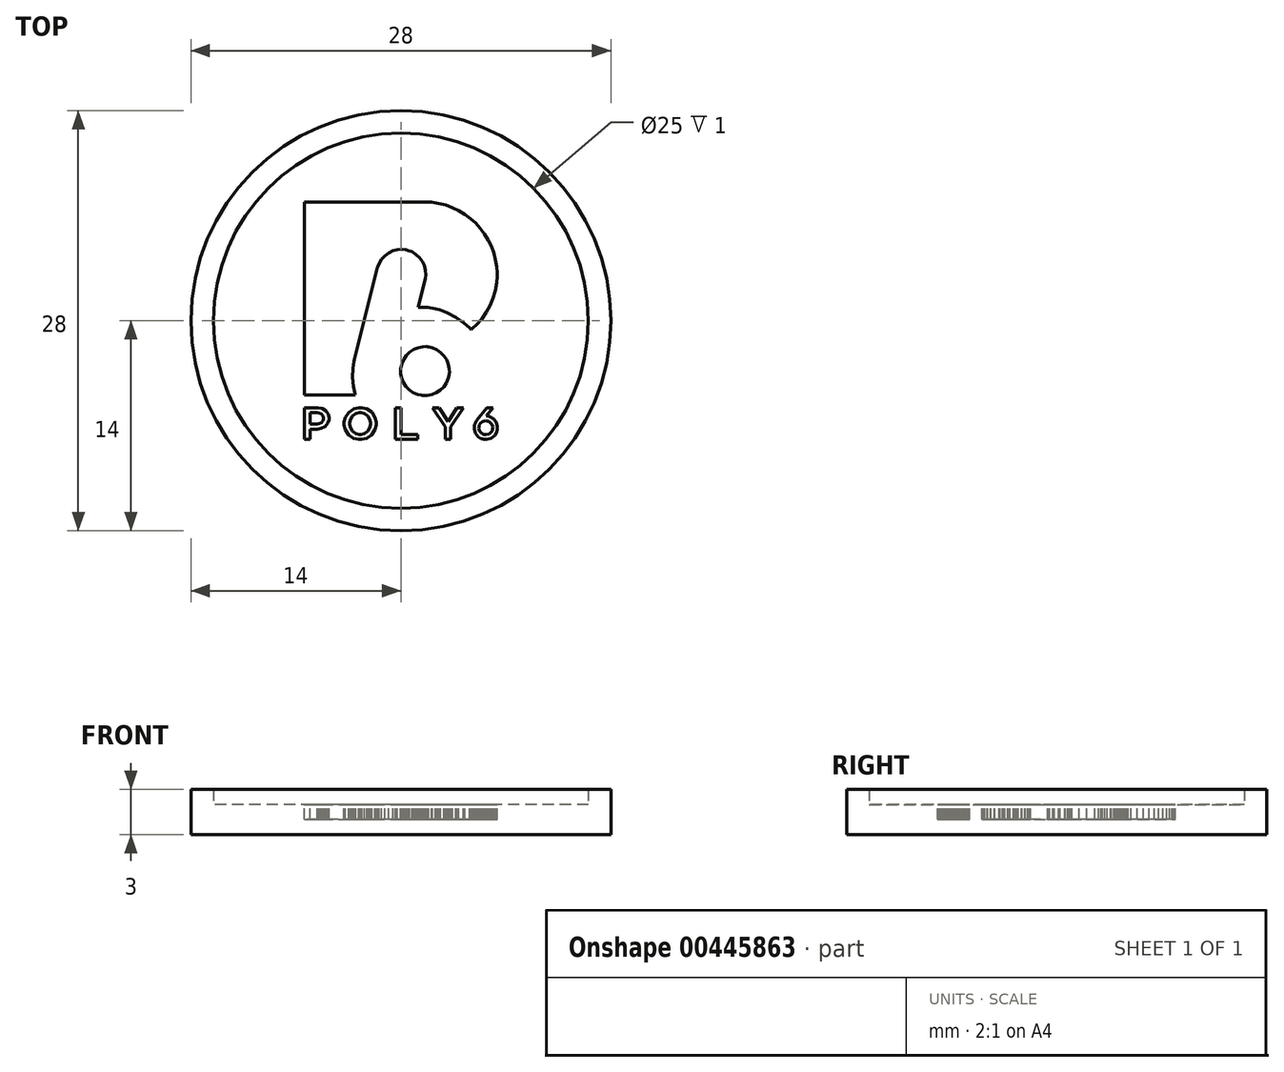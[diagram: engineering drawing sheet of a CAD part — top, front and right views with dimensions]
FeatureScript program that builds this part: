
annotation { "Feature Type Name" : "Feature", "Feature Type Description" : "" }
export const myFeature = defineFeature(function(context is Context, id is Id, definition is map)
    precondition{}
    {
        {
            var Q0;
            Q0=qCreatedBy(makeId("Top.planeOp"),FACE);
            var sketch = newSketch(context, id + "F0", { "sketchPlane" : qUnion([Q0])});
            skCircle(sketch, "E0", {"center": v(0, 0) * mm, "radius": 12.5 * mm});
            skSolve(sketch);
        }
        {
            var Q0;
            Q0=qCreatedBy(makeId("Top.planeOp"),FACE);
            var sketch = newSketch(context, id + "F1", { "sketchPlane" : qUnion([Q0])});
            skLineSegment(sketch, "E1", {"start": v(2.95, -7.92) * mm, "end": v(3.33, -7.92) * mm});
            skLineSegment(sketch, "E2", {"start": v(3.33, -7.92) * mm, "end": v(3.33, -7.07) * mm});
            skLineSegment(sketch, "E3", {"start": v(3.33, -7.07) * mm, "end": v(4.17, -5.8) * mm});
            skLineSegment(sketch, "E4", {"start": v(4.17, -5.8) * mm, "end": v(3.74, -5.8) * mm});
            skLineSegment(sketch, "E5", {"start": v(3.74, -5.8) * mm, "end": v(3.14, -6.73) * mm});
            skLineSegment(sketch, "E6", {"start": v(3.14, -6.73) * mm, "end": v(2.55, -5.8) * mm});
            skLineSegment(sketch, "E7", {"start": v(2.55, -5.8) * mm, "end": v(2.1, -5.8) * mm});
            skLineSegment(sketch, "E8", {"start": v(2.1, -5.8) * mm, "end": v(2.95, -7.08) * mm});
            skLineSegment(sketch, "E9", {"start": v(2.95, -7.08) * mm, "end": v(2.95, -7.92) * mm});
            skLineSegment(sketch, "E10", {"start": v(-0.38, -7.92) * mm, "end": v(1.11, -7.92) * mm});
            skLineSegment(sketch, "E11", {"start": v(1.11, -7.92) * mm, "end": v(1.11, -7.58) * mm});
            skLineSegment(sketch, "E12", {"start": v(1.11, -7.58) * mm, "end": v(0, -7.58) * mm});
            skLineSegment(sketch, "E13", {"start": v(0, -7.58) * mm, "end": v(0, -5.8) * mm});
            skLineSegment(sketch, "E14", {"start": v(0, -5.8) * mm, "end": v(-0.38, -5.8) * mm});
            skLineSegment(sketch, "E15", {"start": v(-0.38, -5.8) * mm, "end": v(-0.38, -7.92) * mm});
            skLineSegment(sketch, "E16", {"start": v(-2.71, -7.59) * mm, "end": v(-2.78, -7.59) * mm});
            skLineSegment(sketch, "E17", {"start": v(-2.78, -7.59) * mm, "end": v(-3, -7.53) * mm});
            skLineSegment(sketch, "E18", {"start": v(-3, -7.53) * mm, "end": v(-3.21, -7.37) * mm});
            skLineSegment(sketch, "E19", {"start": v(-3.21, -7.37) * mm, "end": v(-3.36, -7.14) * mm});
            skLineSegment(sketch, "E20", {"start": v(-3.36, -7.14) * mm, "end": v(-3.4, -6.93) * mm});
            skLineSegment(sketch, "E21", {"start": v(-3.4, -6.93) * mm, "end": v(-3.4, -6.86) * mm});
            skLineSegment(sketch, "E22", {"start": v(-3.4, -6.86) * mm, "end": v(-3.4, -6.85) * mm});
            skLineSegment(sketch, "E23", {"start": v(-3.4, -6.85) * mm, "end": v(-3.4, -6.78) * mm});
            skLineSegment(sketch, "E24", {"start": v(-3.4, -6.78) * mm, "end": v(-3.36, -6.57) * mm});
            skLineSegment(sketch, "E25", {"start": v(-3.36, -6.57) * mm, "end": v(-3.22, -6.34) * mm});
            skLineSegment(sketch, "E26", {"start": v(-3.22, -6.34) * mm, "end": v(-3, -6.19) * mm});
            skLineSegment(sketch, "E27", {"start": v(-3, -6.19) * mm, "end": v(-2.79, -6.13) * mm});
            skLineSegment(sketch, "E28", {"start": v(-2.79, -6.13) * mm, "end": v(-2.72, -6.13) * mm});
            skLineSegment(sketch, "E29", {"start": v(-2.72, -6.13) * mm, "end": v(-2.65, -6.13) * mm});
            skLineSegment(sketch, "E30", {"start": v(-2.65, -6.13) * mm, "end": v(-2.44, -6.19) * mm});
            skLineSegment(sketch, "E31", {"start": v(-2.44, -6.19) * mm, "end": v(-2.22, -6.34) * mm});
            skLineSegment(sketch, "E32", {"start": v(-2.22, -6.34) * mm, "end": v(-2.07, -6.58) * mm});
            skLineSegment(sketch, "E33", {"start": v(-2.07, -6.58) * mm, "end": v(-2.02, -6.79) * mm});
            skLineSegment(sketch, "E34", {"start": v(-2.02, -6.79) * mm, "end": v(-2.02, -6.86) * mm});
            skLineSegment(sketch, "E35", {"start": v(-2.02, -6.86) * mm, "end": v(-2.02, -6.86) * mm});
            skLineSegment(sketch, "E36", {"start": v(-2.02, -6.86) * mm, "end": v(-2.02, -6.93) * mm});
            skLineSegment(sketch, "E37", {"start": v(-2.02, -6.93) * mm, "end": v(-2.07, -7.14) * mm});
            skLineSegment(sketch, "E38", {"start": v(-2.07, -7.14) * mm, "end": v(-2.21, -7.37) * mm});
            skLineSegment(sketch, "E39", {"start": v(-2.21, -7.37) * mm, "end": v(-2.43, -7.53) * mm});
            skLineSegment(sketch, "E40", {"start": v(-2.43, -7.53) * mm, "end": v(-2.64, -7.59) * mm});
            skLineSegment(sketch, "E41", {"start": v(-2.64, -7.59) * mm, "end": v(-2.71, -7.59) * mm});
            skLineSegment(sketch, "E42", {"start": v(-2.72, -7.92) * mm, "end": v(-2.6, -7.92) * mm});
            skLineSegment(sketch, "E43", {"start": v(-2.6, -7.92) * mm, "end": v(-2.28, -7.83) * mm});
            skLineSegment(sketch, "E44", {"start": v(-2.28, -7.83) * mm, "end": v(-1.94, -7.6) * mm});
            skLineSegment(sketch, "E45", {"start": v(-1.94, -7.6) * mm, "end": v(-1.72, -7.27) * mm});
            skLineSegment(sketch, "E46", {"start": v(-1.72, -7.27) * mm, "end": v(-1.64, -6.96) * mm});
            skLineSegment(sketch, "E47", {"start": v(-1.64, -6.96) * mm, "end": v(-1.64, -6.86) * mm});
            skLineSegment(sketch, "E48", {"start": v(-1.64, -6.86) * mm, "end": v(-1.64, -6.85) * mm});
            skLineSegment(sketch, "E49", {"start": v(-1.64, -6.85) * mm, "end": v(-1.64, -6.75) * mm});
            skLineSegment(sketch, "E50", {"start": v(-1.64, -6.75) * mm, "end": v(-1.72, -6.44) * mm});
            skLineSegment(sketch, "E51", {"start": v(-1.72, -6.44) * mm, "end": v(-1.94, -6.1) * mm});
            skLineSegment(sketch, "E52", {"start": v(-1.94, -6.1) * mm, "end": v(-2.28, -5.88) * mm});
            skLineSegment(sketch, "E53", {"start": v(-2.28, -5.88) * mm, "end": v(-2.6, -5.8) * mm});
            skLineSegment(sketch, "E54", {"start": v(-2.6, -5.8) * mm, "end": v(-2.71, -5.8) * mm});
            skLineSegment(sketch, "E55", {"start": v(-2.71, -5.8) * mm, "end": v(-2.82, -5.8) * mm});
            skLineSegment(sketch, "E56", {"start": v(-2.82, -5.8) * mm, "end": v(-3.14, -5.88) * mm});
            skLineSegment(sketch, "E57", {"start": v(-3.14, -5.88) * mm, "end": v(-3.49, -6.11) * mm});
            skLineSegment(sketch, "E58", {"start": v(-3.49, -6.11) * mm, "end": v(-3.7, -6.45) * mm});
            skLineSegment(sketch, "E59", {"start": v(-3.7, -6.45) * mm, "end": v(-3.79, -6.76) * mm});
            skLineSegment(sketch, "E60", {"start": v(-3.79, -6.76) * mm, "end": v(-3.79, -6.86) * mm});
            skLineSegment(sketch, "E61", {"start": v(-3.79, -6.86) * mm, "end": v(-3.79, -6.86) * mm});
            skLineSegment(sketch, "E62", {"start": v(-3.79, -6.86) * mm, "end": v(-3.79, -6.97) * mm});
            skLineSegment(sketch, "E63", {"start": v(-3.79, -6.97) * mm, "end": v(-3.7, -7.27) * mm});
            skLineSegment(sketch, "E64", {"start": v(-3.7, -7.27) * mm, "end": v(-3.49, -7.6) * mm});
            skLineSegment(sketch, "E65", {"start": v(-3.49, -7.6) * mm, "end": v(-3.15, -7.84) * mm});
            skLineSegment(sketch, "E66", {"start": v(-3.15, -7.84) * mm, "end": v(-2.83, -7.92) * mm});
            skLineSegment(sketch, "E67", {"start": v(-2.83, -7.92) * mm, "end": v(-2.72, -7.92) * mm});
            skLineSegment(sketch, "E68", {"start": v(-6.07, -6.9) * mm, "end": v(-6.07, -6.14) * mm});
            skLineSegment(sketch, "E69", {"start": v(-6.07, -6.14) * mm, "end": v(-5.63, -6.14) * mm});
            skLineSegment(sketch, "E70", {"start": v(-5.63, -6.14) * mm, "end": v(-5.58, -6.14) * mm});
            skLineSegment(sketch, "E71", {"start": v(-5.58, -6.14) * mm, "end": v(-5.44, -6.16) * mm});
            skLineSegment(sketch, "E72", {"start": v(-5.44, -6.16) * mm, "end": v(-5.3, -6.23) * mm});
            skLineSegment(sketch, "E73", {"start": v(-5.3, -6.23) * mm, "end": v(-5.2, -6.35) * mm});
            skLineSegment(sketch, "E74", {"start": v(-5.2, -6.35) * mm, "end": v(-5.17, -6.47) * mm});
            skLineSegment(sketch, "E75", {"start": v(-5.17, -6.47) * mm, "end": v(-5.17, -6.52) * mm});
            skLineSegment(sketch, "E76", {"start": v(-5.17, -6.52) * mm, "end": v(-5.17, -6.52) * mm});
            skLineSegment(sketch, "E77", {"start": v(-5.17, -6.52) * mm, "end": v(-5.17, -6.56) * mm});
            skLineSegment(sketch, "E78", {"start": v(-5.17, -6.56) * mm, "end": v(-5.2, -6.67) * mm});
            skLineSegment(sketch, "E79", {"start": v(-5.2, -6.67) * mm, "end": v(-5.3, -6.8) * mm});
            skLineSegment(sketch, "E80", {"start": v(-5.3, -6.8) * mm, "end": v(-5.44, -6.87) * mm});
            skLineSegment(sketch, "E81", {"start": v(-5.44, -6.87) * mm, "end": v(-5.58, -6.9) * mm});
            skLineSegment(sketch, "E82", {"start": v(-5.58, -6.9) * mm, "end": v(-5.63, -6.9) * mm});
            skLineSegment(sketch, "E83", {"start": v(-5.63, -6.9) * mm, "end": v(-6.07, -6.9) * mm});
            skLineSegment(sketch, "E84", {"start": v(-6.44, -7.92) * mm, "end": v(-6.07, -7.92) * mm});
            skLineSegment(sketch, "E85", {"start": v(-6.07, -7.92) * mm, "end": v(-6.07, -7.24) * mm});
            skLineSegment(sketch, "E86", {"start": v(-6.07, -7.24) * mm, "end": v(-5.64, -7.24) * mm});
            skLineSegment(sketch, "E87", {"start": v(-5.64, -7.24) * mm, "end": v(-5.56, -7.24) * mm});
            skLineSegment(sketch, "E88", {"start": v(-5.56, -7.24) * mm, "end": v(-5.31, -7.2) * mm});
            skLineSegment(sketch, "E89", {"start": v(-5.31, -7.2) * mm, "end": v(-5.05, -7.05) * mm});
            skLineSegment(sketch, "E90", {"start": v(-5.05, -7.05) * mm, "end": v(-4.86, -6.83) * mm});
            skLineSegment(sketch, "E91", {"start": v(-4.86, -6.83) * mm, "end": v(-4.8, -6.6) * mm});
            skLineSegment(sketch, "E92", {"start": v(-4.8, -6.6) * mm, "end": v(-4.8, -6.51) * mm});
            skLineSegment(sketch, "E93", {"start": v(-4.8, -6.51) * mm, "end": v(-4.8, -6.5) * mm});
            skLineSegment(sketch, "E94", {"start": v(-4.8, -6.5) * mm, "end": v(-4.8, -6.43) * mm});
            skLineSegment(sketch, "E95", {"start": v(-4.8, -6.43) * mm, "end": v(-4.85, -6.22) * mm});
            skLineSegment(sketch, "E96", {"start": v(-4.85, -6.22) * mm, "end": v(-5.01, -6) * mm});
            skLineSegment(sketch, "E97", {"start": v(-5.01, -6) * mm, "end": v(-5.27, -5.85) * mm});
            skLineSegment(sketch, "E98", {"start": v(-5.27, -5.85) * mm, "end": v(-5.52, -5.8) * mm});
            skLineSegment(sketch, "E99", {"start": v(-5.52, -5.8) * mm, "end": v(-5.6, -5.8) * mm});
            skLineSegment(sketch, "E100", {"start": v(-5.6, -5.8) * mm, "end": v(-6.44, -5.8) * mm});
            skLineSegment(sketch, "E101", {"start": v(-6.44, -5.8) * mm, "end": v(-6.44, -7.92) * mm});
            skLineSegment(sketch, "E102", {"start": v(1.79, -1.74) * mm, "end": v(1.7, -1.73) * mm});
            skLineSegment(sketch, "E103", {"start": v(1.7, -1.73) * mm, "end": v(1.46, -1.74) * mm});
            skLineSegment(sketch, "E104", {"start": v(1.46, -1.74) * mm, "end": v(1.14, -1.8) * mm});
            skLineSegment(sketch, "E105", {"start": v(1.14, -1.8) * mm, "end": v(0.85, -1.92) * mm});
            skLineSegment(sketch, "E106", {"start": v(0.85, -1.92) * mm, "end": v(0.6, -2.09) * mm});
            skLineSegment(sketch, "E107", {"start": v(0.6, -2.09) * mm, "end": v(0.37, -2.3) * mm});
            skLineSegment(sketch, "E108", {"start": v(0.37, -2.3) * mm, "end": v(0.19, -2.56) * mm});
            skLineSegment(sketch, "E109", {"start": v(0.19, -2.56) * mm, "end": v(0.06, -2.86) * mm});
            skLineSegment(sketch, "E110", {"start": v(0.06, -2.86) * mm, "end": v(0, -3.1) * mm});
            skLineSegment(sketch, "E111", {"start": v(0, -3.1) * mm, "end": v(0, -3.18) * mm});
            skLineSegment(sketch, "E112", {"start": v(0, -3.18) * mm, "end": v(-0.02, -3.26) * mm});
            skLineSegment(sketch, "E113", {"start": v(-0.02, -3.26) * mm, "end": v(0, -3.5) * mm});
            skLineSegment(sketch, "E114", {"start": v(0, -3.5) * mm, "end": v(0.05, -3.82) * mm});
            skLineSegment(sketch, "E115", {"start": v(0.05, -3.82) * mm, "end": v(0.17, -4.12) * mm});
            skLineSegment(sketch, "E116", {"start": v(0.17, -4.12) * mm, "end": v(0.34, -4.38) * mm});
            skLineSegment(sketch, "E117", {"start": v(0.34, -4.38) * mm, "end": v(0.56, -4.6) * mm});
            skLineSegment(sketch, "E118", {"start": v(0.56, -4.6) * mm, "end": v(0.82, -4.78) * mm});
            skLineSegment(sketch, "E119", {"start": v(0.82, -4.78) * mm, "end": v(1.11, -4.9) * mm});
            skLineSegment(sketch, "E120", {"start": v(1.11, -4.9) * mm, "end": v(1.35, -4.97) * mm});
            skLineSegment(sketch, "E121", {"start": v(1.35, -4.97) * mm, "end": v(1.43, -4.97) * mm});
            skLineSegment(sketch, "E122", {"start": v(1.43, -4.97) * mm, "end": v(1.52, -4.98) * mm});
            skLineSegment(sketch, "E123", {"start": v(1.52, -4.98) * mm, "end": v(1.76, -4.98) * mm});
            skLineSegment(sketch, "E124", {"start": v(1.76, -4.98) * mm, "end": v(2.08, -4.92) * mm});
            skLineSegment(sketch, "E125", {"start": v(2.08, -4.92) * mm, "end": v(2.37, -4.8) * mm});
            skLineSegment(sketch, "E126", {"start": v(2.37, -4.8) * mm, "end": v(2.63, -4.63) * mm});
            skLineSegment(sketch, "E127", {"start": v(2.63, -4.63) * mm, "end": v(2.85, -4.4) * mm});
            skLineSegment(sketch, "E128", {"start": v(2.85, -4.4) * mm, "end": v(3.03, -4.15) * mm});
            skLineSegment(sketch, "E129", {"start": v(3.03, -4.15) * mm, "end": v(3.16, -3.85) * mm});
            skLineSegment(sketch, "E130", {"start": v(3.16, -3.85) * mm, "end": v(3.22, -3.61) * mm});
            skLineSegment(sketch, "E131", {"start": v(3.22, -3.61) * mm, "end": v(3.23, -3.53) * mm});
            skLineSegment(sketch, "E132", {"start": v(3.23, -3.53) * mm, "end": v(3.24, -3.45) * mm});
            skLineSegment(sketch, "E133", {"start": v(3.24, -3.45) * mm, "end": v(3.23, -3.2) * mm});
            skLineSegment(sketch, "E134", {"start": v(3.23, -3.2) * mm, "end": v(3.17, -2.89) * mm});
            skLineSegment(sketch, "E135", {"start": v(3.17, -2.89) * mm, "end": v(3.05, -2.6) * mm});
            skLineSegment(sketch, "E136", {"start": v(3.05, -2.6) * mm, "end": v(2.88, -2.34) * mm});
            skLineSegment(sketch, "E137", {"start": v(2.88, -2.34) * mm, "end": v(2.66, -2.11) * mm});
            skLineSegment(sketch, "E138", {"start": v(2.66, -2.11) * mm, "end": v(2.4, -1.93) * mm});
            skLineSegment(sketch, "E139", {"start": v(2.4, -1.93) * mm, "end": v(2.1, -1.8) * mm});
            skLineSegment(sketch, "E140", {"start": v(2.1, -1.8) * mm, "end": v(1.87, -1.75) * mm});
            skLineSegment(sketch, "E141", {"start": v(1.87, -1.75) * mm, "end": v(1.79, -1.74) * mm});
            skLineSegment(sketch, "E142", {"start": v(1.56, 7.92) * mm, "end": v(1.68, 7.92) * mm});
            skLineSegment(sketch, "E143", {"start": v(1.68, 7.92) * mm, "end": v(2.05, 7.9) * mm});
            skLineSegment(sketch, "E144", {"start": v(2.05, 7.9) * mm, "end": v(2.53, 7.82) * mm});
            skLineSegment(sketch, "E145", {"start": v(2.53, 7.82) * mm, "end": v(3, 7.7) * mm});
            skLineSegment(sketch, "E146", {"start": v(3, 7.7) * mm, "end": v(3.44, 7.54) * mm});
            skLineSegment(sketch, "E147", {"start": v(3.44, 7.54) * mm, "end": v(3.86, 7.33) * mm});
            skLineSegment(sketch, "E148", {"start": v(3.86, 7.33) * mm, "end": v(4.26, 7.09) * mm});
            skLineSegment(sketch, "E149", {"start": v(4.26, 7.09) * mm, "end": v(4.64, 6.8) * mm});
            skLineSegment(sketch, "E150", {"start": v(4.64, 6.8) * mm, "end": v(4.98, 6.5) * mm});
            skLineSegment(sketch, "E151", {"start": v(4.98, 6.5) * mm, "end": v(5.3, 6.15) * mm});
            skLineSegment(sketch, "E152", {"start": v(5.3, 6.15) * mm, "end": v(5.58, 5.78) * mm});
            skLineSegment(sketch, "E153", {"start": v(5.58, 5.78) * mm, "end": v(5.82, 5.38) * mm});
            skLineSegment(sketch, "E154", {"start": v(5.82, 5.38) * mm, "end": v(6.03, 4.96) * mm});
            skLineSegment(sketch, "E155", {"start": v(6.03, 4.96) * mm, "end": v(6.2, 4.52) * mm});
            skLineSegment(sketch, "E156", {"start": v(6.2, 4.52) * mm, "end": v(6.31, 4.05) * mm});
            skLineSegment(sketch, "E157", {"start": v(6.31, 4.05) * mm, "end": v(6.39, 3.58) * mm});
            skLineSegment(sketch, "E158", {"start": v(6.39, 3.58) * mm, "end": v(6.41, 3.2) * mm});
            skLineSegment(sketch, "E159", {"start": v(6.41, 3.2) * mm, "end": v(6.41, 3.09) * mm});
            skLineSegment(sketch, "E160", {"start": v(6.41, 3.09) * mm, "end": v(6.41, 2.95) * mm});
            skLineSegment(sketch, "E161", {"start": v(6.41, 2.95) * mm, "end": v(6.38, 2.54) * mm});
            skLineSegment(sketch, "E162", {"start": v(6.38, 2.54) * mm, "end": v(6.3, 2) * mm});
            skLineSegment(sketch, "E163", {"start": v(6.3, 2) * mm, "end": v(6.14, 1.5) * mm});
            skLineSegment(sketch, "E164", {"start": v(6.14, 1.5) * mm, "end": v(5.95, 1.02) * mm});
            skLineSegment(sketch, "E165", {"start": v(5.95, 1.02) * mm, "end": v(5.7, 0.56) * mm});
            skLineSegment(sketch, "E166", {"start": v(5.7, 0.56) * mm, "end": v(5.4, 0.14) * mm});
            skLineSegment(sketch, "E167", {"start": v(5.4, 0.14) * mm, "end": v(5.06, -0.25) * mm});
            skLineSegment(sketch, "E168", {"start": v(5.06, -0.25) * mm, "end": v(4.78, -0.52) * mm});
            skLineSegment(sketch, "E169", {"start": v(4.78, -0.52) * mm, "end": v(4.68, -0.6) * mm});
            skLineSegment(sketch, "E170", {"start": v(4.68, -0.6) * mm, "end": v(4.58, -0.48) * mm});
            skLineSegment(sketch, "E171", {"start": v(4.58, -0.48) * mm, "end": v(4.21, -0.15) * mm});
            skLineSegment(sketch, "E172", {"start": v(4.21, -0.15) * mm, "end": v(3.67, 0.24) * mm});
            skLineSegment(sketch, "E173", {"start": v(3.67, 0.24) * mm, "end": v(3.07, 0.54) * mm});
            skLineSegment(sketch, "E174", {"start": v(3.07, 0.54) * mm, "end": v(2.58, 0.72) * mm});
            skLineSegment(sketch, "E175", {"start": v(2.58, 0.72) * mm, "end": v(2.42, 0.76) * mm});
            skLineSegment(sketch, "E176", {"start": v(2.42, 0.76) * mm, "end": v(2.31, 0.79) * mm});
            skLineSegment(sketch, "E177", {"start": v(2.31, 0.79) * mm, "end": v(1.78, 0.87) * mm});
            skLineSegment(sketch, "E178", {"start": v(1.78, 0.87) * mm, "end": v(1.26, 0.9) * mm});
            skLineSegment(sketch, "E179", {"start": v(1.26, 0.9) * mm, "end": v(1.15, 0.9) * mm});
            skLineSegment(sketch, "E180", {"start": v(1.15, 0.9) * mm, "end": v(1.61, 2.7) * mm});
            skLineSegment(sketch, "E181", {"start": v(1.61, 2.7) * mm, "end": v(1.63, 2.79) * mm});
            skLineSegment(sketch, "E182", {"start": v(1.63, 2.79) * mm, "end": v(1.66, 3.04) * mm});
            skLineSegment(sketch, "E183", {"start": v(1.66, 3.04) * mm, "end": v(1.64, 3.36) * mm});
            skLineSegment(sketch, "E184", {"start": v(1.64, 3.36) * mm, "end": v(1.56, 3.67) * mm});
            skLineSegment(sketch, "E185", {"start": v(1.56, 3.67) * mm, "end": v(1.43, 3.95) * mm});
            skLineSegment(sketch, "E186", {"start": v(1.43, 3.95) * mm, "end": v(1.24, 4.2) * mm});
            skLineSegment(sketch, "E187", {"start": v(1.24, 4.2) * mm, "end": v(1, 4.42) * mm});
            skLineSegment(sketch, "E188", {"start": v(1, 4.42) * mm, "end": v(0.73, 4.59) * mm});
            skLineSegment(sketch, "E189", {"start": v(0.73, 4.59) * mm, "end": v(0.5, 4.68) * mm});
            skLineSegment(sketch, "E190", {"start": v(0.5, 4.68) * mm, "end": v(0.42, 4.7) * mm});
            skLineSegment(sketch, "E191", {"start": v(0.42, 4.7) * mm, "end": v(0.34, 4.72) * mm});
            skLineSegment(sketch, "E192", {"start": v(0.34, 4.72) * mm, "end": v(0.09, 4.75) * mm});
            skLineSegment(sketch, "E193", {"start": v(0.09, 4.75) * mm, "end": v(-0.23, 4.73) * mm});
            skLineSegment(sketch, "E194", {"start": v(-0.23, 4.73) * mm, "end": v(-0.54, 4.65) * mm});
            skLineSegment(sketch, "E195", {"start": v(-0.54, 4.65) * mm, "end": v(-0.83, 4.52) * mm});
            skLineSegment(sketch, "E196", {"start": v(-0.83, 4.52) * mm, "end": v(-1.08, 4.33) * mm});
            skLineSegment(sketch, "E197", {"start": v(-1.08, 4.33) * mm, "end": v(-1.3, 4.1) * mm});
            skLineSegment(sketch, "E198", {"start": v(-1.3, 4.1) * mm, "end": v(-1.46, 3.82) * mm});
            skLineSegment(sketch, "E199", {"start": v(-1.46, 3.82) * mm, "end": v(-1.55, 3.59) * mm});
            skLineSegment(sketch, "E200", {"start": v(-1.55, 3.59) * mm, "end": v(-1.57, 3.5) * mm});
            skLineSegment(sketch, "E201", {"start": v(-1.57, 3.5) * mm, "end": v(-3.1, -2.58) * mm});
            skLineSegment(sketch, "E202", {"start": v(-3.1, -2.58) * mm, "end": v(-3.1, -2.58) * mm});
            skLineSegment(sketch, "E203", {"start": v(-3.1, -2.58) * mm, "end": v(-3.14, -2.73) * mm});
            skLineSegment(sketch, "E204", {"start": v(-3.14, -2.73) * mm, "end": v(-3.2, -3.19) * mm});
            skLineSegment(sketch, "E205", {"start": v(-3.2, -3.19) * mm, "end": v(-3.23, -3.79) * mm});
            skLineSegment(sketch, "E206", {"start": v(-3.23, -3.79) * mm, "end": v(-3.17, -4.38) * mm});
            skLineSegment(sketch, "E207", {"start": v(-3.17, -4.38) * mm, "end": v(-3.08, -4.81) * mm});
            skLineSegment(sketch, "E208", {"start": v(-3.08, -4.81) * mm, "end": v(-3.04, -4.95) * mm});
            skLineSegment(sketch, "E209", {"start": v(-3.04, -4.95) * mm, "end": v(-6.44, -4.95) * mm});
            skLineSegment(sketch, "E210", {"start": v(-6.44, -4.95) * mm, "end": v(-6.44, 7.92) * mm});
            skLineSegment(sketch, "E211", {"start": v(-6.44, 7.92) * mm, "end": v(1.56, 7.92) * mm});
            skLineSegment(sketch, "E212", {"start": v(6.1, -7.28) * mm, "end": v(6.1, -7.32) * mm});
            skLineSegment(sketch, "E213", {"start": v(6.1, -7.32) * mm, "end": v(6.02, -7.44) * mm});
            skLineSegment(sketch, "E214", {"start": v(6.02, -7.44) * mm, "end": v(5.88, -7.55) * mm});
            skLineSegment(sketch, "E215", {"start": v(5.88, -7.55) * mm, "end": v(5.7, -7.6) * mm});
            skLineSegment(sketch, "E216", {"start": v(5.7, -7.6) * mm, "end": v(5.57, -7.6) * mm});
            skLineSegment(sketch, "E217", {"start": v(5.57, -7.6) * mm, "end": v(5.53, -7.58) * mm});
            skLineSegment(sketch, "E218", {"start": v(5.53, -7.58) * mm, "end": v(5.48, -7.57) * mm});
            skLineSegment(sketch, "E219", {"start": v(5.48, -7.57) * mm, "end": v(5.36, -7.5) * mm});
            skLineSegment(sketch, "E220", {"start": v(5.36, -7.5) * mm, "end": v(5.25, -7.36) * mm});
            skLineSegment(sketch, "E221", {"start": v(5.25, -7.36) * mm, "end": v(5.2, -7.19) * mm});
            skLineSegment(sketch, "E222", {"start": v(5.2, -7.19) * mm, "end": v(5.2, -7.05) * mm});
            skLineSegment(sketch, "E223", {"start": v(5.2, -7.05) * mm, "end": v(5.22, -7) * mm});
            skLineSegment(sketch, "E224", {"start": v(5.22, -7) * mm, "end": v(5.23, -6.96) * mm});
            skLineSegment(sketch, "E225", {"start": v(5.23, -6.96) * mm, "end": v(5.3, -6.84) * mm});
            skLineSegment(sketch, "E226", {"start": v(5.3, -6.84) * mm, "end": v(5.45, -6.73) * mm});
            skLineSegment(sketch, "E227", {"start": v(5.45, -6.73) * mm, "end": v(5.62, -6.68) * mm});
            skLineSegment(sketch, "E228", {"start": v(5.62, -6.68) * mm, "end": v(5.76, -6.68) * mm});
            skLineSegment(sketch, "E229", {"start": v(5.76, -6.68) * mm, "end": v(5.8, -6.7) * mm});
            skLineSegment(sketch, "E230", {"start": v(5.8, -6.7) * mm, "end": v(5.84, -6.71) * mm});
            skLineSegment(sketch, "E231", {"start": v(5.84, -6.71) * mm, "end": v(5.96, -6.78) * mm});
            skLineSegment(sketch, "E232", {"start": v(5.96, -6.78) * mm, "end": v(6.07, -6.92) * mm});
            skLineSegment(sketch, "E233", {"start": v(6.07, -6.92) * mm, "end": v(6.12, -7.1) * mm});
            skLineSegment(sketch, "E234", {"start": v(6.12, -7.1) * mm, "end": v(6.12, -7.23) * mm});
            skLineSegment(sketch, "E235", {"start": v(6.12, -7.23) * mm, "end": v(6.1, -7.28) * mm});
            skLineSegment(sketch, "E236", {"start": v(5.9, -6.4) * mm, "end": v(5.88, -6.39) * mm});
            skLineSegment(sketch, "E237", {"start": v(5.88, -6.39) * mm, "end": v(5.7, -6.36) * mm});
            skLineSegment(sketch, "E238", {"start": v(5.7, -6.36) * mm, "end": v(5.7, -6.36) * mm});
            skLineSegment(sketch, "E239", {"start": v(5.7, -6.36) * mm, "end": v(6.15, -5.8) * mm});
            skLineSegment(sketch, "E240", {"start": v(6.15, -5.8) * mm, "end": v(5.72, -5.8) * mm});
            skLineSegment(sketch, "E241", {"start": v(5.72, -5.8) * mm, "end": v(5.07, -6.64) * mm});
            skLineSegment(sketch, "E242", {"start": v(5.07, -6.64) * mm, "end": v(5.07, -6.64) * mm});
            skLineSegment(sketch, "E243", {"start": v(5.07, -6.64) * mm, "end": v(5.03, -6.69) * mm});
            skLineSegment(sketch, "E244", {"start": v(5.03, -6.69) * mm, "end": v(5.03, -6.69) * mm});
            skLineSegment(sketch, "E245", {"start": v(5.03, -6.69) * mm, "end": v(5.02, -6.7) * mm});
            skLineSegment(sketch, "E246", {"start": v(5.02, -6.7) * mm, "end": v(4.92, -6.89) * mm});
            skLineSegment(sketch, "E247", {"start": v(4.92, -6.89) * mm, "end": v(4.92, -6.9) * mm});
            skLineSegment(sketch, "E248", {"start": v(4.92, -6.9) * mm, "end": v(4.9, -6.98) * mm});
            skLineSegment(sketch, "E249", {"start": v(4.9, -6.98) * mm, "end": v(4.89, -7.22) * mm});
            skLineSegment(sketch, "E250", {"start": v(4.89, -7.22) * mm, "end": v(4.97, -7.5) * mm});
            skLineSegment(sketch, "E251", {"start": v(4.97, -7.5) * mm, "end": v(5.16, -7.74) * mm});
            skLineSegment(sketch, "E252", {"start": v(5.16, -7.74) * mm, "end": v(5.36, -7.86) * mm});
            skLineSegment(sketch, "E253", {"start": v(5.36, -7.86) * mm, "end": v(5.43, -7.88) * mm});
            skLineSegment(sketch, "E254", {"start": v(5.43, -7.88) * mm, "end": v(5.5, -7.9) * mm});
            skLineSegment(sketch, "E255", {"start": v(5.5, -7.9) * mm, "end": v(5.74, -7.92) * mm});
            skLineSegment(sketch, "E256", {"start": v(5.74, -7.92) * mm, "end": v(6.03, -7.83) * mm});
            skLineSegment(sketch, "E257", {"start": v(6.03, -7.83) * mm, "end": v(6.26, -7.64) * mm});
            skLineSegment(sketch, "E258", {"start": v(6.26, -7.64) * mm, "end": v(6.39, -7.44) * mm});
            skLineSegment(sketch, "E259", {"start": v(6.39, -7.44) * mm, "end": v(6.4, -7.37) * mm});
            skLineSegment(sketch, "E260", {"start": v(6.4, -7.37) * mm, "end": v(6.43, -7.3) * mm});
            skLineSegment(sketch, "E261", {"start": v(6.43, -7.3) * mm, "end": v(6.44, -7.06) * mm});
            skLineSegment(sketch, "E262", {"start": v(6.44, -7.06) * mm, "end": v(6.35, -6.78) * mm});
            skLineSegment(sketch, "E263", {"start": v(6.35, -6.78) * mm, "end": v(6.16, -6.54) * mm});
            skLineSegment(sketch, "E264", {"start": v(6.16, -6.54) * mm, "end": v(5.96, -6.42) * mm});
            skLineSegment(sketch, "E265", {"start": v(5.96, -6.42) * mm, "end": v(5.9, -6.4) * mm});
            skSolve(sketch);
        }
        {
            var Q0;
            Q0=makeQuery(id+"F0.imprint","IMPRINT",FACE,{"disambiguationData":[TD([[makeQuery(id+"F0.imprint","IMPRINT",EDGE,{"derivedFrom":sQuery(id+"F0.wireOp",EDGE,"E0")}),1.0]])]});
            extrude(context, id + "F2", {"entities" : qUnion([Q0]), "oppositeDirection" : true, "depth" : 2 * mm});
        }
        {
            var Q0;
            Q0=makeQuery(id+"F1.imprint","IMPRINT",FACE,{"disambiguationData":[TD([[makeQuery(id+"F1.imprint","IMPRINT",EDGE,{"derivedFrom":sQuery(id+"F1.wireOp",EDGE,"E142")}),-1.0]])]});
            var Q1;
            Q1=makeQuery(id+"F1.imprint","IMPRINT",FACE,{"disambiguationData":[TD([[makeQuery(id+"F1.imprint","IMPRINT",EDGE,{"derivedFrom":sQuery(id+"F1.wireOp",EDGE,"E102")}),1.0]])]});
            var Q2;
            Q2=makeQuery(id+"F1.imprint","IMPRINT",FACE,{"disambiguationData":[TD([[makeQuery(id+"F1.imprint","IMPRINT",EDGE,{"derivedFrom":sQuery(id+"F1.wireOp",EDGE,"E212")}),1.0]])]});
            var Q3;
            Q3=makeQuery(id+"F1.imprint","IMPRINT",FACE,{"disambiguationData":[TD([[makeQuery(id+"F1.imprint","IMPRINT",EDGE,{"derivedFrom":sQuery(id+"F1.wireOp",EDGE,"E1")}),1.0]])]});
            var Q4;
            Q4=makeQuery(id+"F1.imprint","IMPRINT",FACE,{"disambiguationData":[TD([[makeQuery(id+"F1.imprint","IMPRINT",EDGE,{"derivedFrom":sQuery(id+"F1.wireOp",EDGE,"E10")}),1.0]])]});
            var Q5;
            Q5=makeQuery(id+"F1.imprint","IMPRINT",FACE,{"disambiguationData":[TD([[makeQuery(id+"F1.imprint","IMPRINT",EDGE,{"derivedFrom":sQuery(id+"F1.wireOp",EDGE,"E68")}),1.0]])]});
            var Q6;
            Q6=makeQuery(id+"F1.imprint","IMPRINT",FACE,{"disambiguationData":[TD([[makeQuery(id+"F1.imprint","IMPRINT",EDGE,{"derivedFrom":sQuery(id+"F1.wireOp",EDGE,"E16")}),1.0]])]});
            extrude(context, id + "F3", {"entities" : qUnion([Q0, Q1, Q2, Q3, Q4, Q5, Q6]), "operationType" : NewBodyOperationType.REMOVE, "oppositeDirection" : true, "depth" : 1 * mm});
        }
        {
            var Q0;
            Q0=qCreatedBy(makeId("Top.planeOp"),FACE);
            var sketch = newSketch(context, id + "F4", { "sketchPlane" : qUnion([Q0])});
            skCircle(sketch, "E266", {"center": v(0, 0) * mm, "radius": 14 * mm});
            skCircle(sketch, "E267", {"center": v(0, 0) * mm, "radius": 12.5 * mm});
            skSolve(sketch);
        }
        {
            var Q0;
            Q0 = qSketchRegion(id + "F4", true);
            extrude(context, id + "F5", {"entities" : qUnion([Q0]), "operationType" : NewBodyOperationType.ADD, "depth" : 1 * mm, "hasSecondDirection" : true, "secondDirectionOppositeDirection" : true, "secondDirectionDepth" : 2 * mm});
        }
    });
